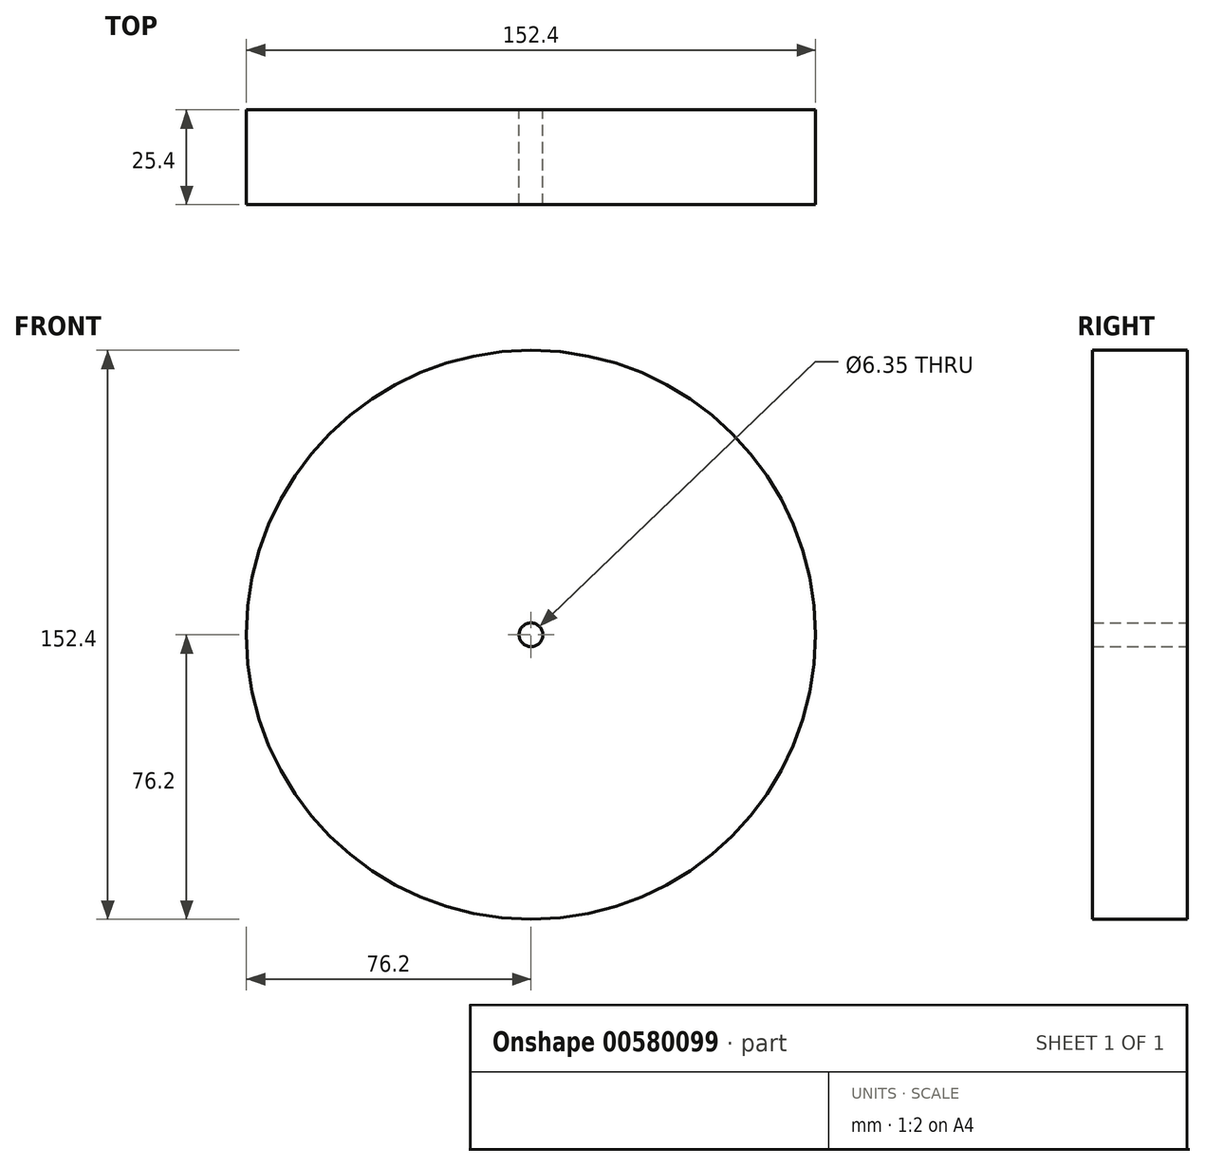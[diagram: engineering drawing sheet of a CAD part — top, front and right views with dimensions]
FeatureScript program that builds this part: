
annotation { "Feature Type Name" : "Feature", "Feature Type Description" : "" }
export const myFeature = defineFeature(function(context is Context, id is Id, definition is map)
    precondition{}
    {
        {
            var Q0;
            Q0=qCreatedBy(makeId("Front.planeOp"),FACE);
            var sketch = newSketch(context, id + "F0", { "sketchPlane" : qUnion([Q0])});
            skCircle(sketch, "E0", {"center": v(0, 0) * mm, "radius": 76.2 * mm});
            skCircle(sketch, "E1", {"center": v(0, 0) * mm, "radius": 3.18 * mm});
            skSolve(sketch);
        }
        {
            var Q0;
            Q0=qSketchRegion(id+"F0",true);
            extrude(context, id + "F1", {"entities" : qUnion([Q0]), "depth" : 25.4 * mm, "symmetric" : true});
        }
    });
